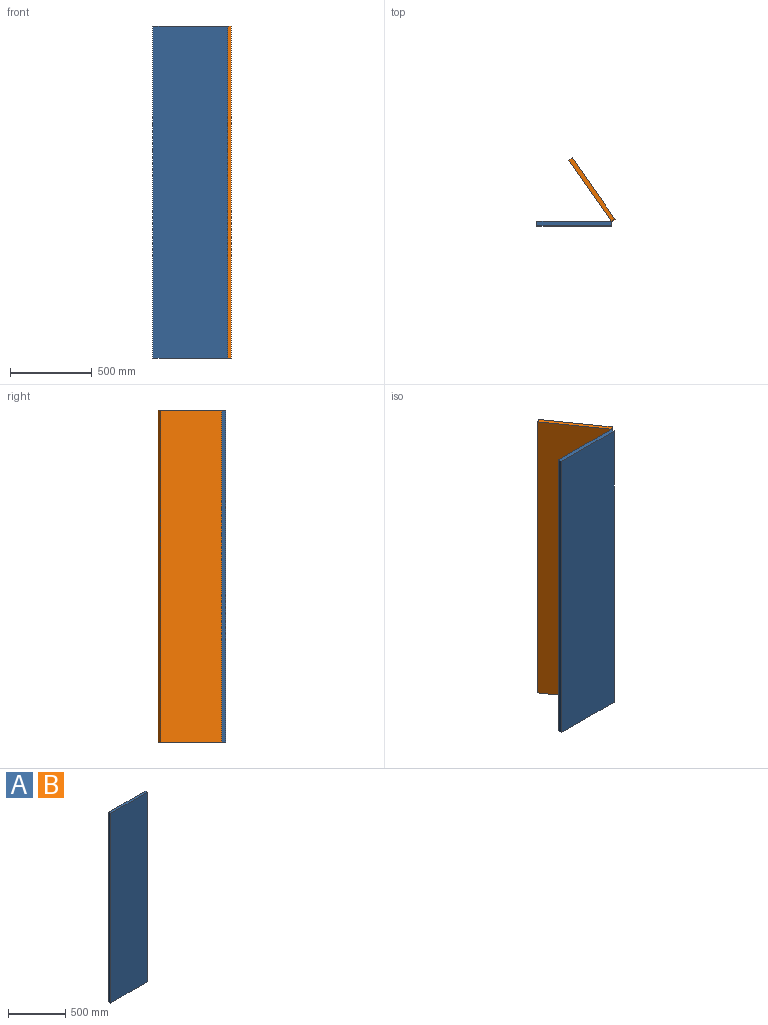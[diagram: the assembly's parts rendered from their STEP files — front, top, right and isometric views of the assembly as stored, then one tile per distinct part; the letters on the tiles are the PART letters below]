
ASSEMBLY  parts=2 mates=1
PART A: 6 faces, bbox 457.2x25.4x2032 mm
  f0: plane 457.2x25.4mm, normal (0,0,1), area 11612.9mm2, adj f1,f3,f4,f5
  f1: plane 2032x25.4mm, normal (-1,0,0), area 51612.8mm2, adj f0,f2,f4,f5
  f2: plane 457.2x25.4mm, normal (0,0,-1), area 11612.9mm2, adj f1,f3,f4,f5
  f3: plane 2032x25.4mm, normal (1,0,0), area 51612.8mm2, adj f0,f2,f4,f5
  f4: plane 2032x457.2mm, normal (0,-1,0), area 929030.4mm2, adj f0,f1,f2,f3
  f5: plane 2032x457.2mm, normal (0,1,0), area 929030.4mm2, adj f0,f1,f2,f3
PART B: same geometry as A
PLACE A at identity fixed
PLACE B rot(axis=(0,0,1),125deg) t=(97.48,187.26,0)mm
MATE revolute A.f0 <-> B.f0  axis (0,0,-1) through (228.6,0,1016)mm
